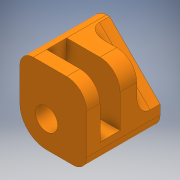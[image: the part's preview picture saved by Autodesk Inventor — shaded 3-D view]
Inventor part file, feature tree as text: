
AUTODESK INVENTOR PART (.ipt)
format: ipt  version: 2017 (Build 210142000, 142)  size: 245,760 bytes
history: native  units: mm
features: extrude x10, sketch x10, fillet x3
ambient origin geometry x8: Origin, YZ Plane, XZ Plane, XY Plane, X Axis, Y Axis, Z Axis, Center Point
bodies: Solid1 (feature_tree)
feature tree (23):
  extrude  "Extrusion1"  Depth=3.0mm
  extrude  "Extrusion2"  Depth=3.0mm
  extrude  "Extrusion3"  Depth=0.5mm TaperAngle=0.0deg
  fillet  "Fillet1"  Radius=2.0mm
  sketch  "Sketch5"  dims[d10=2.0mm d11=2.0mm]
  sketch  "Sketch7"  dims[d12=3.3333mm d15=5.8mm]
  extrude  "Extrusion8"  Depth=2.0mm
  extrude  "Extrusion10"  Depth=5.8mm
  extrude  "Extrusion11"  Depth=5.5mm TaperAngle=0.0deg
  extrude  "Extrusion12"  Depth=0.25mm TaperAngle=0.0deg
  fillet  "Fillet3"  Radius=0.25mm
  extrude  "Extrusion14"  Depth=0.2mm TaperAngle=0.0deg
  extrude  "Extrusion15"  Depth=2.0mm
  extrude  "Extrusion16"  [1 undecoded]
  fillet  "Fillet5"  [1 undecoded]
  sketch  "Sketch1"  dims[d0=5.0mm d1=3.0mm]
  sketch  "Sketch2"  dims[d2=4.0mm d3=3.0mm]
  sketch  "Sketch3"  dims[d4=5.5mm d5=0.0mm d6=0.5mm d7=0.0mm d8=2.0mm d9=0.0mm]
  sketch  "Sketch11"  dims[d25=5.5mm d26=0.0mm d30=1.3mm d31=0.0mm]
  sketch  "Sketch12"  dims[d32=6.0mm d33=0.0mm d34=1.0mm d35=0.0mm d36=0.25mm]
  sketch  "Sketch14"  dims[d41=0.3mm d42=0.0mm d43=0.2mm d44=0.0mm]
  sketch  "Sketch15"  dims[d45=0.2mm d46=0.0mm d47=2.0mm]
  sketch  "Sketch16"  dims[d48=2.0mm d49=0.0mm]
note: 2 required parameter values undecoded (feature->parameter linkage not recoverable at this tier; creation-order binding heuristic only, values carry confidence <= 0.55)
